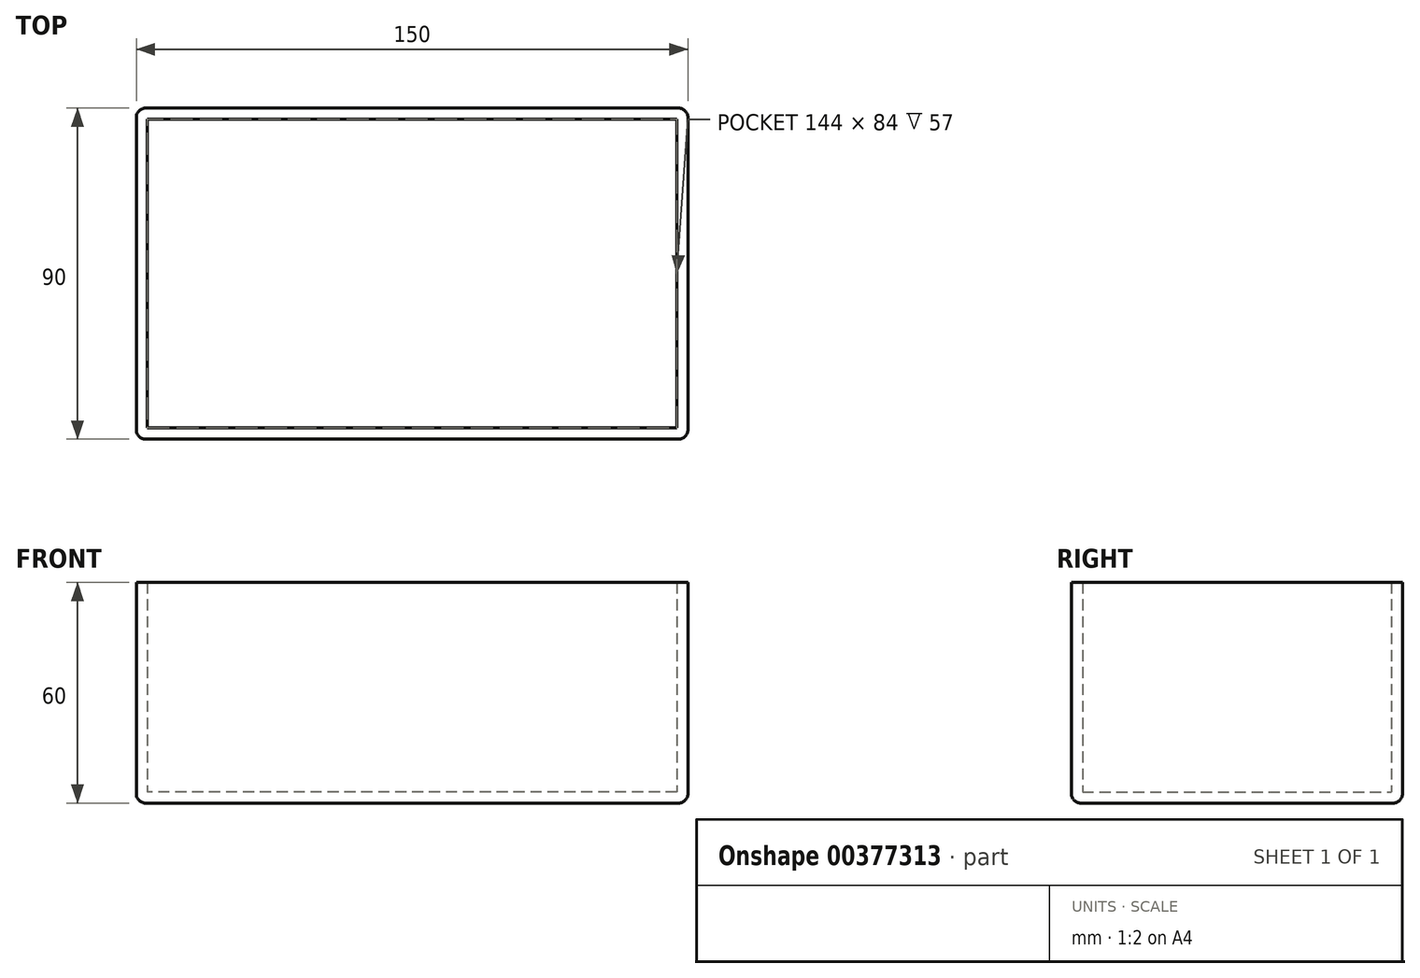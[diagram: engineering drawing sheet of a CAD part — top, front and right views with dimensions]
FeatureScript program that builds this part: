
annotation { "Feature Type Name" : "Feature", "Feature Type Description" : "" }
export const myFeature = defineFeature(function(context is Context, id is Id, definition is map)
    precondition{}
    {
        {
            var Q0;
            Q0=qCreatedBy(makeId("Top.planeOp"),FACE);
            var sketch = newSketch(context, id + "F0", { "sketchPlane" : qUnion([Q0])});
            skLineSegment(sketch, "E0.bottom", {"start": v(0, 0) * mm, "end": v(-150, 0) * mm});
            skLineSegment(sketch, "E0.top", {"start": v(0, 90) * mm, "end": v(-150, 90) * mm});
            skLineSegment(sketch, "E0.left", {"start": v(0, 0) * mm, "end": v(0, 90) * mm});
            skLineSegment(sketch, "E0.right", {"start": v(-150, 0) * mm, "end": v(-150, 90) * mm});
            skSolve(sketch);
        }
        {
            var Q0;
            Q0 = qSketchRegion(id + "F0", true);
            extrude(context, id + "F1", {"entities" : qUnion([Q0]), "depth" : 60 * mm});
        }
        {
            var Q0;
            Q0=makeQuery(id+"F1.opExtrude","CAP_FACE",FACE,{"disambiguationData":[OSD([sQuery(id+"F0.wireOp",EDGE,"E0.bottom"),sQuery(id+"F0.wireOp",EDGE,"E0.top"),sQuery(id+"F0.wireOp",EDGE,"E0.left"),sQuery(id+"F0.wireOp",EDGE,"E0.right")])],"isStart":false});
            shell(context, id + "F2", {"entities" : qUnion([Q0]), "thickness" : 3 * mm});
        }
        {
            var Q0;
            Q0=makeQuery(id+"F1.opExtrude","CAP_FACE",FACE,{"disambiguationData":[OSD([sQuery(id+"F0.wireOp",EDGE,"E0.bottom"),sQuery(id+"F0.wireOp",EDGE,"E0.top"),sQuery(id+"F0.wireOp",EDGE,"E0.left"),sQuery(id+"F0.wireOp",EDGE,"E0.right")])],"isStart":true});
            var Q1;
            Q1=makeQuery(id+"F1.opExtrude","SWEPT_EDGE",EDGE,{"disambiguationData":[OSD([sQuery(id+"F0.wireOp",EDGE,"E0.top"),sQuery(id+"F0.wireOp",EDGE,"E0.left")])]});
            var Q2;
            Q2=makeQuery(id+"F1.opExtrude","SWEPT_EDGE",EDGE,{"disambiguationData":[OSD([sQuery(id+"F0.wireOp",EDGE,"E0.top"),sQuery(id+"F0.wireOp",EDGE,"E0.right")])]});
            var Q3;
            Q3=makeQuery(id+"F1.opExtrude","SWEPT_EDGE",EDGE,{"disambiguationData":[OSD([sQuery(id+"F0.wireOp",EDGE,"E0.bottom"),sQuery(id+"F0.wireOp",EDGE,"E0.right")])]});
            var Q4;
            Q4=makeQuery(id+"F1.opExtrude","SWEPT_EDGE",EDGE,{"disambiguationData":[OSD([sQuery(id+"F0.wireOp",EDGE,"E0.bottom"),sQuery(id+"F0.wireOp",EDGE,"E0.left")])]});
            fillet(context, id + "F3", {"entities" : qUnion([Q0, Q1, Q2, Q3, Q4]), "radius" : 2.5 * mm, "tangentPropagation" : true, "allowEdgeOverflow" : false});
        }
    });
